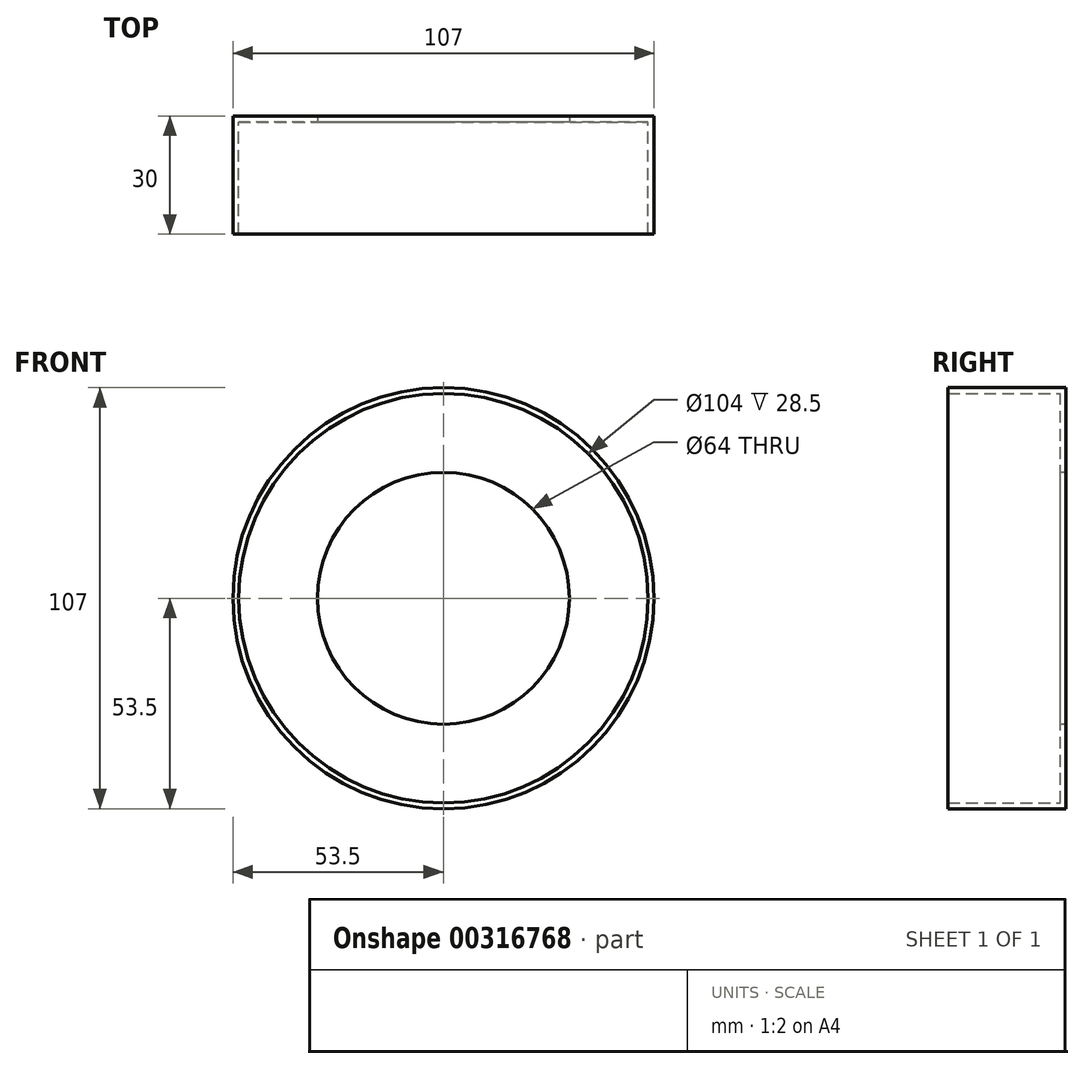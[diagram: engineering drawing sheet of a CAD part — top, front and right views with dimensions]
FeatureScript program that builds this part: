
annotation { "Feature Type Name" : "Feature", "Feature Type Description" : "" }
export const myFeature = defineFeature(function(context is Context, id is Id, definition is map)
    precondition{}
    {
        {
            var Q0;
            Q0=qCreatedBy(makeId("Front.planeOp"),FACE);
            var sketch = newSketch(context, id + "F0", { "sketchPlane" : qUnion([Q0])});
            skCircle(sketch, "E0", {"center": v(0, 0) * mm, "radius": 51.5 * mm});
            skCircle(sketch, "E1", {"center": v(0, 0) * mm, "radius": 53.5 * mm});
            skSolve(sketch);
        }
        {
            var Q0;
            Q0=makeQuery(id+"F0.imprint","IMPRINT",FACE,{"disambiguationData":[TD([[makeQuery(id+"F0.imprint","IMPRINT",EDGE,{"derivedFrom":sQuery(id+"F0.wireOp",EDGE,"E0")}),1.0]])]});
            var Q1;
            Q1=makeQuery(id+"F0.imprint","IMPRINT",FACE,{"disambiguationData":[TD([[makeQuery(id+"F0.imprint","IMPRINT",EDGE,{"derivedFrom":sQuery(id+"F0.wireOp",EDGE,"E0")}),-1.0]])]});
            extrude(context, id + "F1", {"entities" : qUnion([Q0, Q1]), "depth" : 30 * mm});
        }
        {
            var Q0;
            Q0=makeQuery(id+"F1.opExtrude","CAP_FACE",FACE,{"disambiguationData":[OSD([sQuery(id+"F0.wireOp",EDGE,"E1")])],"isStart":false});
            shell(context, id + "F2", {"entities" : qUnion([Q0]), "thickness" : 1.5 * mm});
        }
        {
            var Q0;
            {var subQ0=sQuery(id+"F0.wireOp",EDGE,"E1");Q0=makeQuery(id+"F2.opShell","OFFSET_FACE",FACE,{"disambiguationData":[OSD([subQ0]),TDD([makeQuery(id+"F1.opExtrude","CAP_FACE",FACE,{"disambiguationData":[OSD([subQ0])],"isStart":true})])]});}
            var sketch = newSketch(context, id + "F3", { "sketchPlane" : qUnion([Q0])});
            skCircle(sketch, "E2", {"center": v(0, 0) * mm, "radius": 32 * mm});
            skSolve(sketch);
        }
        {
            var Q0;
            Q0=makeQuery(id+"F3.imprint","IMPRINT",FACE,{"disambiguationData":[TD([[makeQuery(id+"F3.imprint","IMPRINT",EDGE,{"derivedFrom":sQuery(id+"F3.wireOp",EDGE,"E2")}),1.0]])]});
            extrude(context, id + "F4", {"entities" : qUnion([Q0]), "operationType" : NewBodyOperationType.REMOVE, "oppositeDirection" : true, "depth" : 25 * mm});
        }
    });
